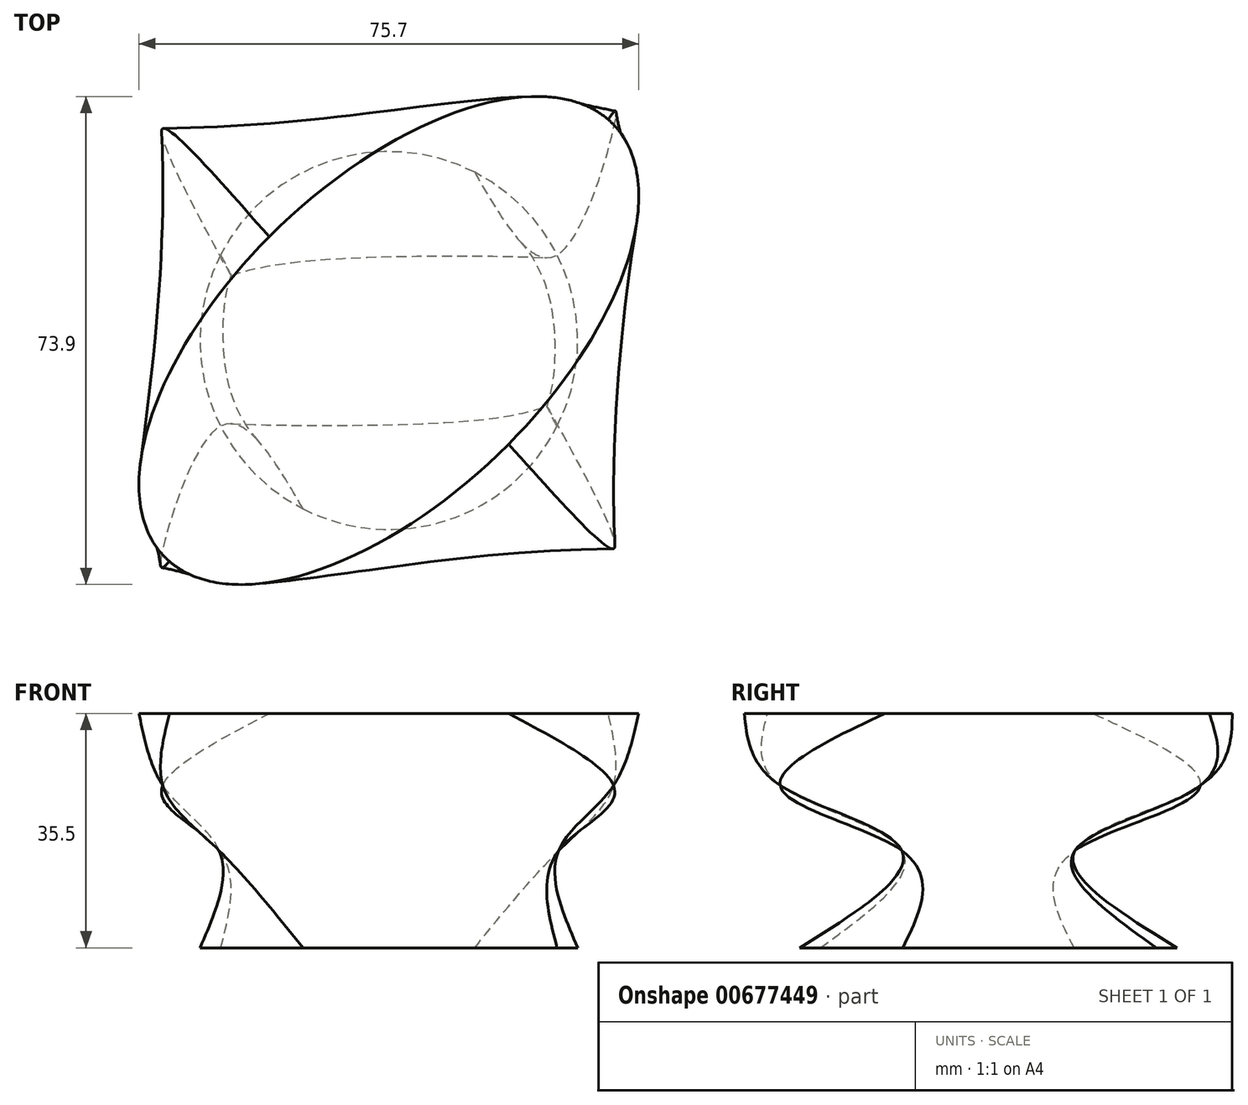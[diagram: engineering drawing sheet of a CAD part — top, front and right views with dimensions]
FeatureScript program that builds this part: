
annotation { "Feature Type Name" : "Feature", "Feature Type Description" : "" }
export const myFeature = defineFeature(function(context is Context, id is Id, definition is map)
    precondition{}
    {
        {
            var Q0;
            Q0=qCreatedBy(makeId("Top.planeOp"),FACE);
            cPlane(context, id + "F0", {"entities" : qUnion([Q0]), "cplaneType" : CPlaneType.OFFSET, "offset" : 26.7 * mm, "width" : 150 * mm, "height" : 150 * mm});
        }
        {
            var Q0;
            Q0=qCreatedBy(makeId("Top.planeOp"),FACE);
            cPlane(context, id + "F1", {"entities" : qUnion([Q0]), "cplaneType" : CPlaneType.OFFSET, "offset" : 47.5 * mm, "width" : 150 * mm, "height" : 150 * mm});
        }
        {
            var Q0;
            Q0=qCreatedBy(makeId("Top.planeOp"),FACE);
            cPlane(context, id + "F2", {"entities" : qUnion([Q0]), "cplaneType" : CPlaneType.OFFSET, "offset" : 12 * mm, "width" : 150 * mm, "height" : 150 * mm});
        }
        {
            var Q0;
            Q0=qCreatedBy(makeId("Top.planeOp"),FACE);
            cPlane(context, id + "F3", {"entities" : qUnion([Q0]), "cplaneType" : CPlaneType.OFFSET, "offset" : 36.6 * mm, "width" : 150 * mm, "height" : 150 * mm});
        }
        {
            var Q0;
            Q0=qCreatedBy(id+"F2.planeOp",FACE);
            var sketch = newSketch(context, id + "F4", { "sketchPlane" : qUnion([Q0])});
            skCircle(sketch, "E0", {"center": v(0, 0) * mm, "radius": 28.6 * mm});
            skSolve(sketch);
        }
        {
            var Q0;
            Q0=qCreatedBy(id+"F0.planeOp",FACE);
            var sketch = newSketch(context, id + "F5", { "sketchPlane" : qUnion([Q0])});
            skLineSegment(sketch, "E1.bottom", {"start": v(25.7, -13.1) * mm, "end": v(-25.7, -13.1) * mm});
            skLineSegment(sketch, "E1.top", {"start": v(25.7, 13.1) * mm, "end": v(-25.7, 13.1) * mm});
            skLineSegment(sketch, "E1.left", {"start": v(25.7, -13.1) * mm, "end": v(25.7, 13.1) * mm});
            skLineSegment(sketch, "E1.right", {"start": v(-25.7, -13.1) * mm, "end": v(-25.7, 13.1) * mm});
            skPoint(sketch, "E1.middle", {"position": v(0, 0) * mm});
            skSolve(sketch);
        }
        {
            var Q0;
            Q0=qCreatedBy(id+"F3.planeOp",FACE);
            var sketch = newSketch(context, id + "F6", { "sketchPlane" : qUnion([Q0])});
            skLineSegment(sketch, "E2.bottom", {"start": v(34.04, -31.52) * mm, "end": v(-34.23, -31.52) * mm});
            skLineSegment(sketch, "E2.top", {"start": v(34.04, 32.1) * mm, "end": v(-34.23, 32.1) * mm});
            skLineSegment(sketch, "E2.left", {"start": v(34.04, -31.52) * mm, "end": v(34.04, 32.1) * mm});
            skLineSegment(sketch, "E2.right", {"start": v(-34.23, -31.52) * mm, "end": v(-34.23, 32.1) * mm});
            skPoint(sketch, "E2.middle", {"position": v(-0.1, 0.3) * mm});
            skSolve(sketch);
        }
        {
            var Q0;
            Q0=qCreatedBy(id+"F1.planeOp",FACE);
            var sketch = newSketch(context, id + "F7", { "sketchPlane" : qUnion([Q0])});
            skEllipse(sketch, "E3", {"center": v(0, 0) * mm, "majorRadius": 47.2 * mm, "minorRadius": 23.9 * mm, "majorAxis": v(0.72, 0.7)});
            skSolve(sketch);
        }
        {
            var Q0;
            Q0=makeQuery(id+"F4.imprint","IMPRINT",FACE,{"disambiguationData":[TD([[makeQuery(id+"F4.imprint","IMPRINT",EDGE,{"derivedFrom":sQuery(id+"F4.wireOp",EDGE,"E0")}),1.0]])]});
            var Q1;
            Q1=makeQuery(id+"F5.imprint","IMPRINT",FACE,{"disambiguationData":[TD([[makeQuery(id+"F5.imprint","IMPRINT",EDGE,{"derivedFrom":sQuery(id+"F5.wireOp",EDGE,"E1.bottom")}),-1.0]])]});
            var Q2;
            Q2=makeQuery(id+"F6.imprint","IMPRINT",FACE,{"disambiguationData":[TD([[makeQuery(id+"F6.imprint","IMPRINT",EDGE,{"derivedFrom":sQuery(id+"F6.wireOp",EDGE,"E2.bottom")}),-1.0]])]});
            var Q3;
            Q3=makeQuery(id+"F7.imprint","IMPRINT",FACE,{"disambiguationData":[TD([[makeQuery(id+"F7.imprint","IMPRINT",EDGE,{"derivedFrom":sQuery(id+"F7.wireOp",EDGE,"E3")}),1.0]])]});
            loft(context, id + "F8", {"sheetProfilesArray" : [{ "sheetProfileEntities" : qUnion([Q0]) }, { "sheetProfileEntities" : qUnion([Q1]) }, { "sheetProfileEntities" : qUnion([Q2]) }, { "sheetProfileEntities" : qUnion([Q3]) }]});
        }
    });
